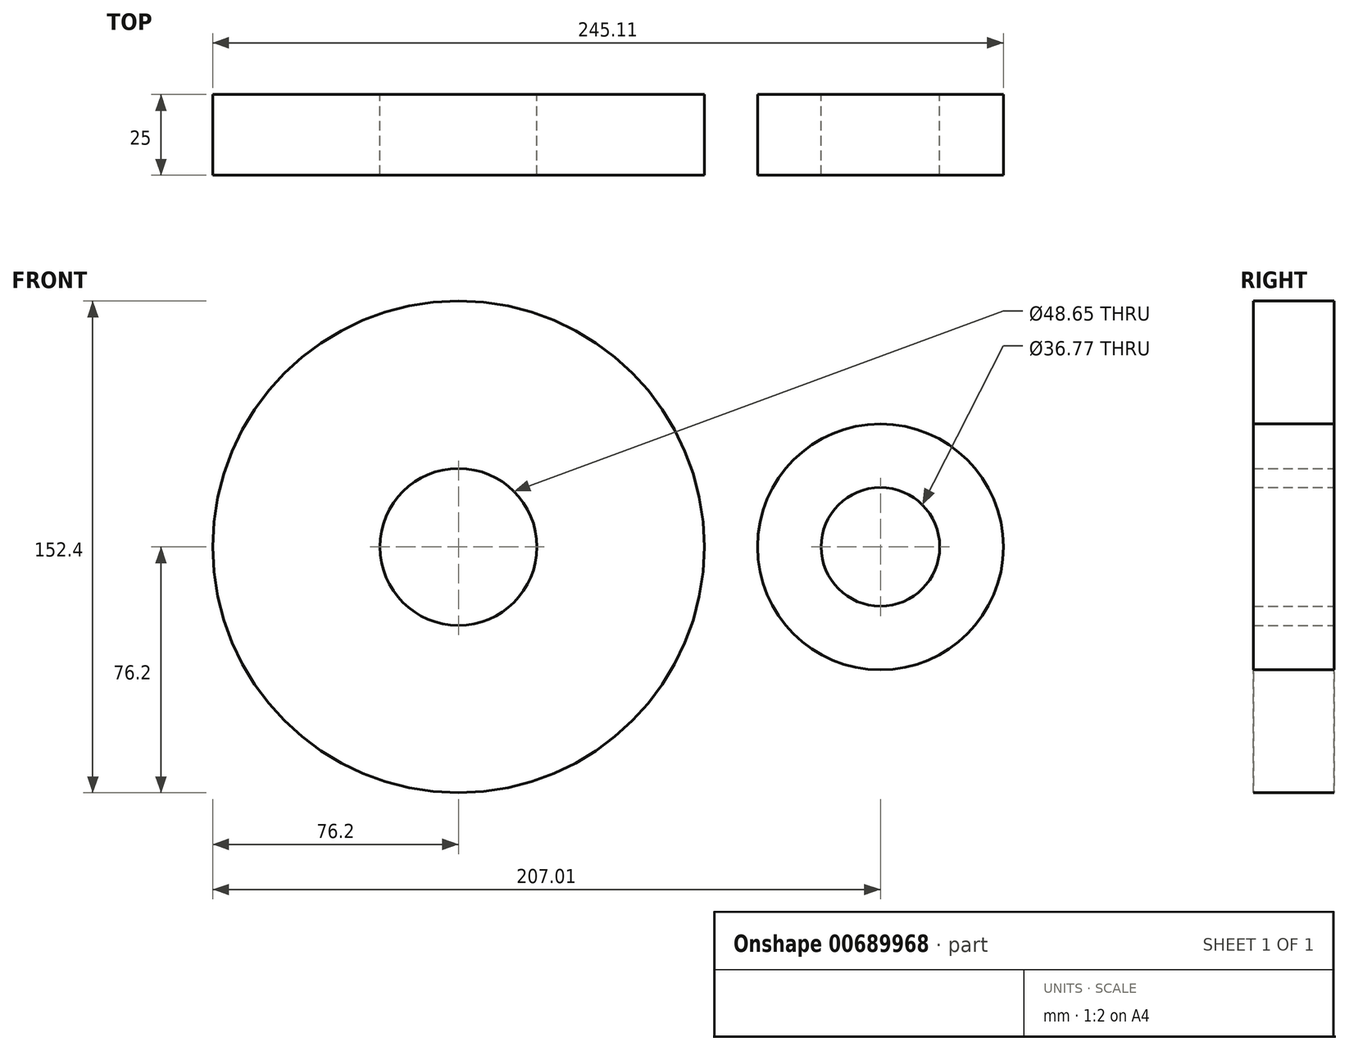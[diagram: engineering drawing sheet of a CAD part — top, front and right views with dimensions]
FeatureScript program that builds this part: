
annotation { "Feature Type Name" : "Feature", "Feature Type Description" : "" }
export const myFeature = defineFeature(function(context is Context, id is Id, definition is map)
    precondition{}
    {
        {
            var Q0;
            Q0=qCreatedBy(makeId("Front.planeOp"),FACE);
            var sketch = newSketch(context, id + "F0", { "sketchPlane" : qUnion([Q0])});
            skCircle(sketch, "E0", {"center": v(0, 0) * mm, "radius": 76.2 * mm});
            skCircle(sketch, "E1", {"center": v(130.8, 0) * mm, "radius": 38.1 * mm});
            skLineSegment(sketch, "E2", {"start": v(22.2, 72.9) * mm, "end": v(141.9, 36.45) * mm});
            skLineSegment(sketch, "E3", {"start": v(0, -76.2) * mm, "end": v(130.81, -39.57) * mm});
            skCircle(sketch, "E4", {"center": v(0, 0) * mm, "radius": 24.32 * mm});
            skCircle(sketch, "E5", {"center": v(130.8, 0) * mm, "radius": 18.39 * mm});
            skSolve(sketch);
        }
        {
            var Q0;
            Q0 = qSketchRegion(id + "F0", true);
            extrude(context, id + "F1", {"entities" : qUnion([Q0]), "depth" : 25 * mm, "offsetDistance" : 25.4 * mm});
        }
    });
